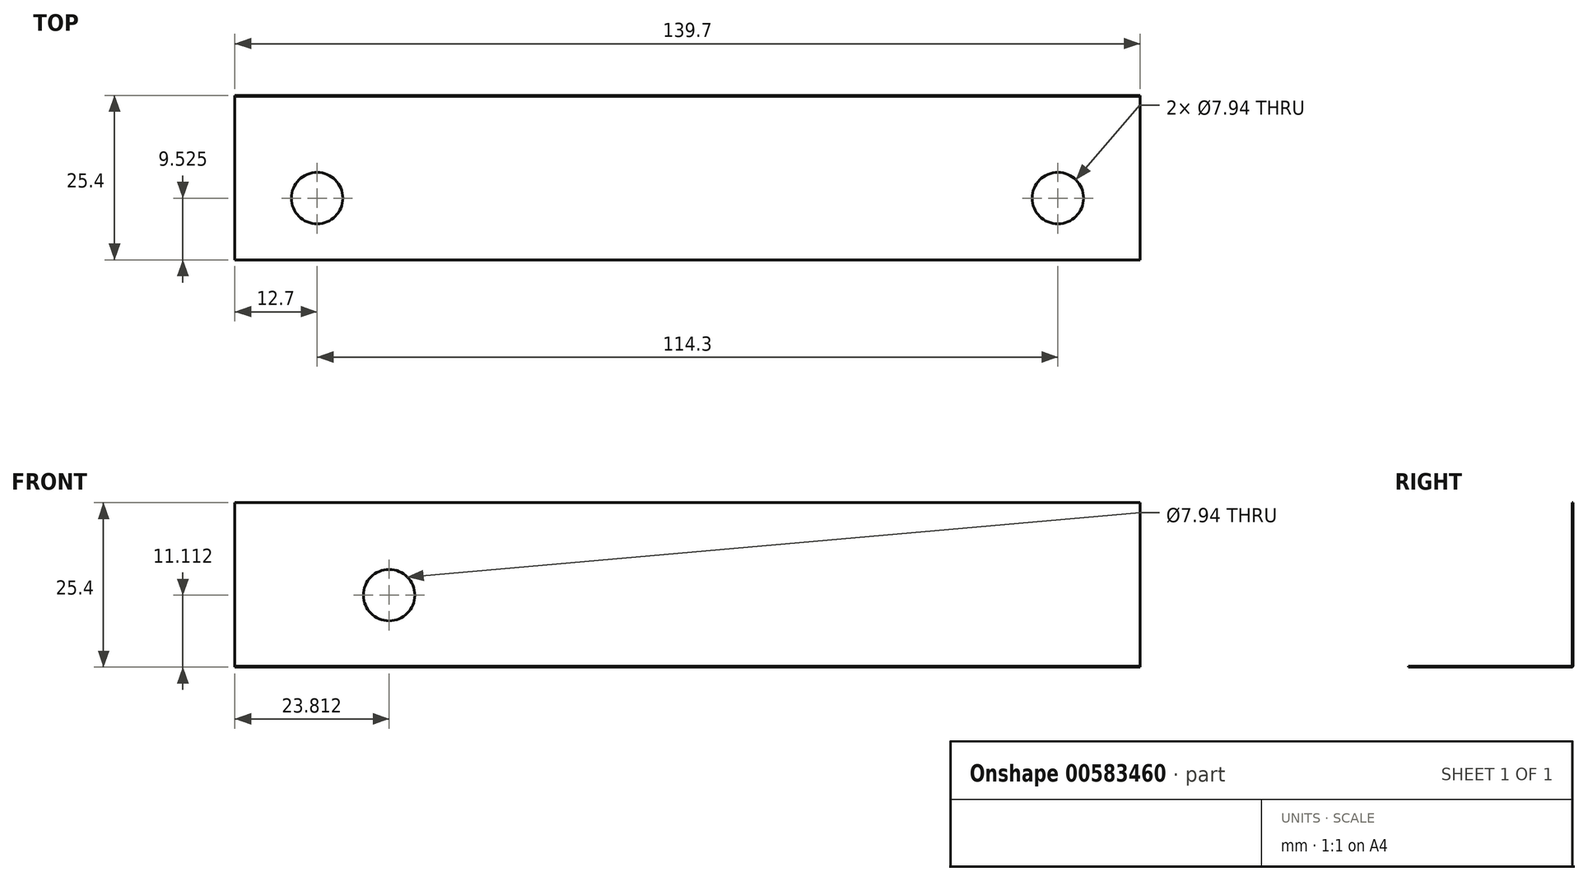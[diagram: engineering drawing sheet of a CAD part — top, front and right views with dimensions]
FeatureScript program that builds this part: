
annotation { "Feature Type Name" : "Feature", "Feature Type Description" : "" }
export const myFeature = defineFeature(function(context is Context, id is Id, definition is map)
    precondition{}
    {
        {
            assignVariable(context, id + "F0", {"name" : "Thickness", "anyValue" : 0.12});
        }
        {
            var Q0;
            Q0=qCreatedBy(makeId("Front.planeOp"),FACE);
            var sketch = newSketch(context, id + "F1", { "sketchPlane" : qUnion([Q0])});
            skLineSegment(sketch, "E0.bottom", {"start": v(69.85, -12.7) * mm, "end": v(-69.85, -12.7) * mm});
            skLineSegment(sketch, "E0.top", {"start": v(69.85, 12.7) * mm, "end": v(-69.85, 12.7) * mm});
            skLineSegment(sketch, "E0.left", {"start": v(69.85, -12.7) * mm, "end": v(69.85, 12.7) * mm});
            skLineSegment(sketch, "E0.right", {"start": v(-69.85, -12.7) * mm, "end": v(-69.85, 12.7) * mm});
            skPoint(sketch, "E0.middle", {"position": v(0, 0) * mm});
            skSolve(sketch);
        }
        {
            var Q0;
            Q0=qSketchRegion(id+"F1",true);
            extrude(context, id + "F2", {"entities" : qUnion([Q0]), "depth" : (getVariable(context, 'Thickness')) * mm});
        }
        {
            var Q0;
            Q0=makeQuery(id+"F2.opExtrude","SWEPT_FACE",FACE,{"disambiguationData":[OSD([sQuery(id+"F1.wireOp",EDGE,"E0.bottom")])]});
            var sketch = newSketch(context, id + "F3", { "sketchPlane" : qUnion([Q0])});
            skLineSegment(sketch, "E1.bottom", {"start": v(-69.85, 0) * mm, "end": v(69.85, 0) * mm});
            skLineSegment(sketch, "E1.top", {"start": v(-69.85, 25.4) * mm, "end": v(69.85, 25.4) * mm});
            skLineSegment(sketch, "E1.left", {"start": v(-69.85, 0) * mm, "end": v(-69.85, 25.4) * mm});
            skLineSegment(sketch, "E1.right", {"start": v(69.85, 0) * mm, "end": v(69.85, 25.4) * mm});
            skSolve(sketch);
        }
        {
            var Q0;
            Q0=qSketchRegion(id+"F3",true);
            extrude(context, id + "F4", {"entities" : qUnion([Q0]), "operationType" : NewBodyOperationType.ADD, "oppositeDirection" : true, "depth" : (getVariable(context, 'Thickness')) * mm});
        }
        {
            var Q0;
            Q0=makeQuery(id+"F2.opExtrude","CAP_FACE",FACE,{"disambiguationData":[OSD([sQuery(id+"F1.wireOp",EDGE,"E0.bottom"),sQuery(id+"F1.wireOp",EDGE,"E0.top"),sQuery(id+"F1.wireOp",EDGE,"E0.left"),sQuery(id+"F1.wireOp",EDGE,"E0.right")])],"isStart":false});
            var sketch = newSketch(context, id + "F5", { "sketchPlane" : qUnion([Q0])});
            skCircle(sketch, "E2", {"center": v(-46.04, -1.59) * mm, "radius": 3.97 * mm});
            skSolve(sketch);
        }
        {
            var Q0;
            Q0=qSketchRegion(id+"F5",true);
            extrude(context, id + "F6", {"entities" : qUnion([Q0]), "operationType" : NewBodyOperationType.REMOVE, "oppositeDirection" : true, "depth" : (getVariable(context, 'Thickness')) * mm});
        }
        {
            var Q0;
            Q0=makeQuery(id+"F4.boolean.opBoolean","MERGE",FACE,{"derivedFrom":[makeQuery(id+"F2.opExtrude","SWEPT_FACE",FACE,{"disambiguationData":[OSD([sQuery(id+"F1.wireOp",EDGE,"E0.bottom")])]}),makeQuery(id+"F4.opExtrude","CAP_FACE",FACE,{"disambiguationData":[OSD([sQuery(id+"F3.wireOp",EDGE,"E1.bottom"),sQuery(id+"F3.wireOp",EDGE,"E1.top"),sQuery(id+"F3.wireOp",EDGE,"E1.left"),sQuery(id+"F3.wireOp",EDGE,"E1.right")])],"isStart":true})]});
            var sketch = newSketch(context, id + "F7", { "sketchPlane" : qUnion([Q0])});
            skCircle(sketch, "E3", {"center": v(-57.15, 15.87) * mm, "radius": 3.97 * mm});
            skCircle(sketch, "E4", {"center": v(57.15, 15.88) * mm, "radius": 3.97 * mm});
            skSolve(sketch);
        }
        {
            var Q0;
            Q0=qSketchRegion(id+"F7",true);
            extrude(context, id + "F8", {"entities" : qUnion([Q0]), "operationType" : NewBodyOperationType.REMOVE, "oppositeDirection" : true, "depth" : (getVariable(context, 'Thickness')) * mm});
        }
        {
            var Q0;
            Q0=makeQuery(id+"F2.opExtrude","CAP_EDGE",EDGE,{"disambiguationData":[OSD([sQuery(id+"F1.wireOp",EDGE,"E0.bottom")])],"isStart":true});
            fillet(context, id + "F9", {"entities" : qUnion([Q0]), "radius" : (getVariable(context, 'Thickness')) * mm, "tangentPropagation" : true, "allowEdgeOverflow" : false});
        }
    });
